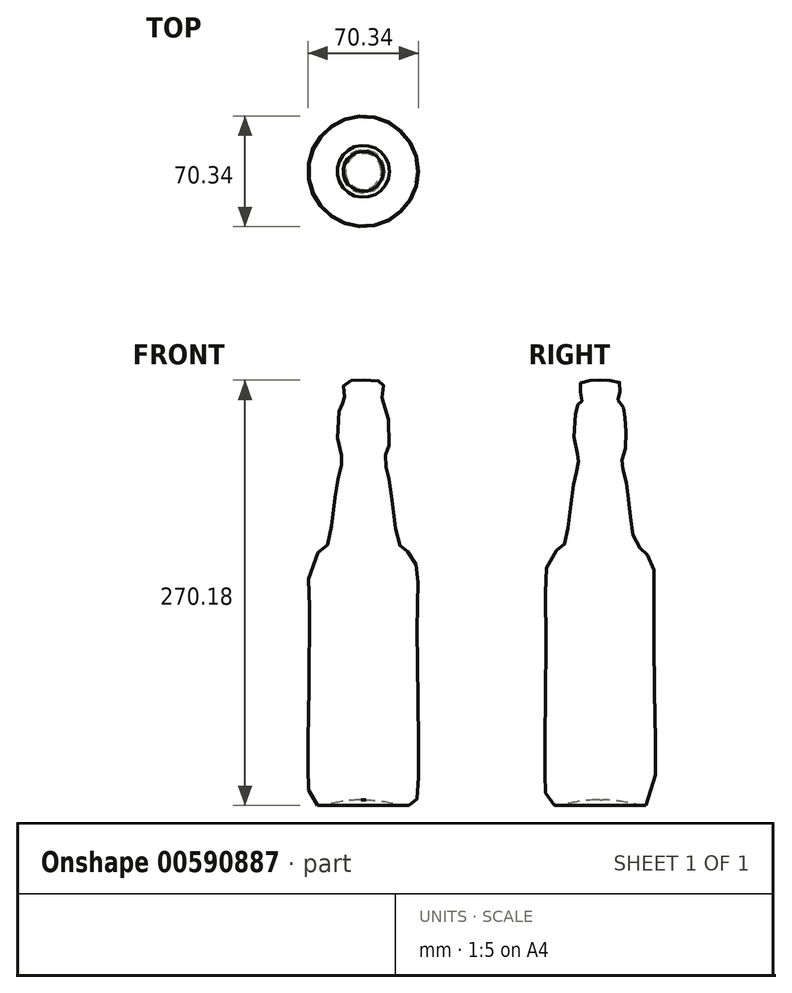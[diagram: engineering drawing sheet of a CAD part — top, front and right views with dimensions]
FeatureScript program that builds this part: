
annotation { "Feature Type Name" : "Feature", "Feature Type Description" : "" }
export const myFeature = defineFeature(function(context is Context, id is Id, definition is map)
    precondition{}
    {
        {
            var Q0;
            Q0=qCreatedBy(makeId("Front.planeOp"),FACE);
            var sketch = newSketch(context, id + "F0", { "sketchPlane" : qUnion([Q0])});
            skPoint(sketch, "E0", {"position": v(0, -3.83) * mm});
            skLineSegment(sketch, "E1", {"start": v(0, 0) * mm, "end": v(0, 270) * mm});
            skFitSpline(sketch, "E2", {"points": [v(0, 3.4) * mm, v(30.88, 0) * mm, v(34.5, 7.4) * mm, v(34.5, 82.5) * mm, v(34.5, 133.09) * mm, v(32.83, 154.43) * mm, v(25.42, 163.41) * mm, v(22.3, 166.54) * mm, v(17.01, 202.92) * mm, v(14.47, 213.49) * mm, v(14.1, 222.5) * mm, v(15.54, 224.51) * mm, v(14.1, 254.18) * mm, v(11.61, 256.33) * mm, v(11.92, 259.33) * mm, v(12.65, 267.62) * mm, v(11.61, 269.17) * mm, v(0, 270) * mm], "startDerivative": vector(481.74, 13.78) * mm, "endDerivative": vector(-247.07, 2.77) * mm});
            skSolve(sketch);
        }
        {
            var Q0;
            {var subQ0=sQuery(id+"F0.wireOp",EDGE,"E2");Q0=makeQuery(id+"F0.imprint","IMPRINT",FACE,{"disambiguationData":[TD([[makeQuery(id+"F0.imprint","IMPRINT",EDGE,{"derivedFrom":subQ0}),1.0]])]});}
            var Q1;
            Q1=sQuery(id+"F0.wireOp",EDGE,"E1");
            revolve(context, id + "F1", {"entities" : qUnion([Q0]), "axis" : qUnion([Q1]), "revolveType" : RevolveType.FULL});
        }
    });
